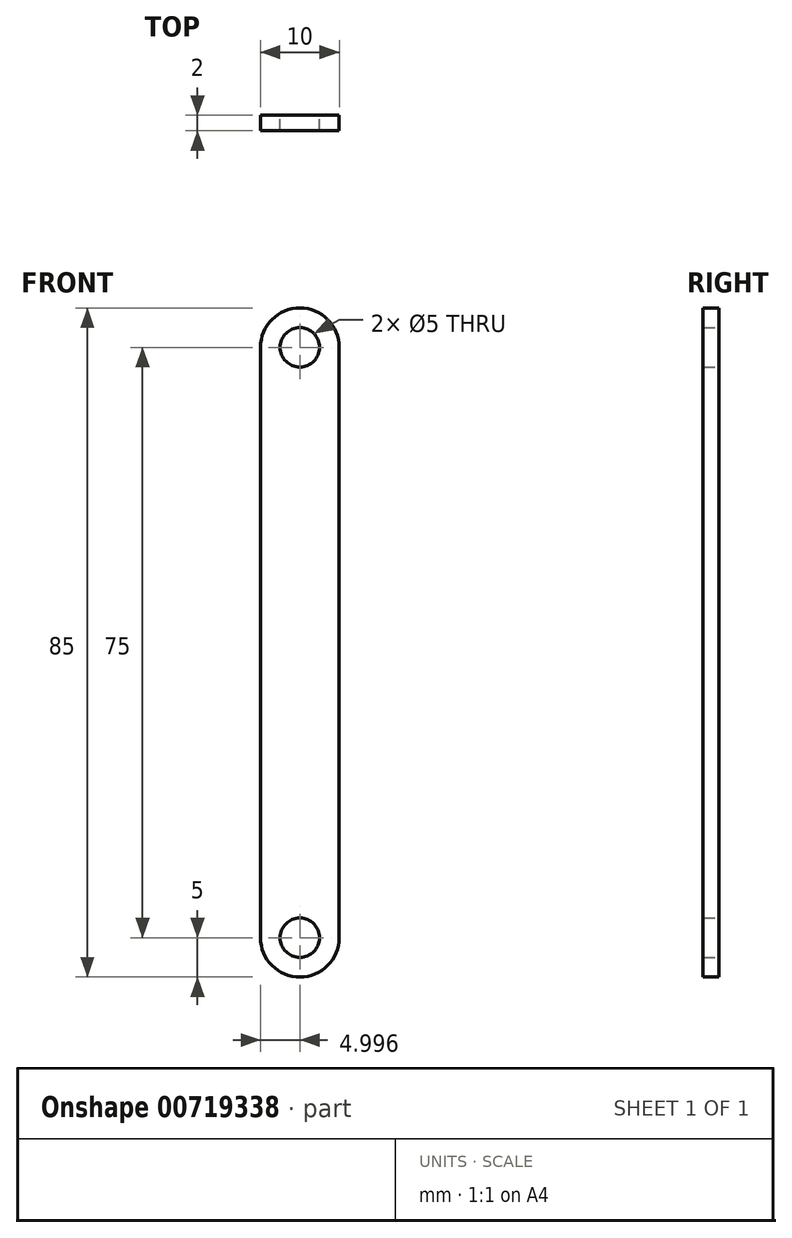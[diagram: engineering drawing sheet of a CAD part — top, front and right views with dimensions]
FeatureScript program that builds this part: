
annotation { "Feature Type Name" : "Feature", "Feature Type Description" : "" }
export const myFeature = defineFeature(function(context is Context, id is Id, definition is map)
    precondition{}
    {
        {
            var Q0;
            Q0=qCreatedBy(makeId("Front.planeOp"),FACE);
            var sketch = newSketch(context, id + "F0", { "sketchPlane" : qUnion([Q0])});
            skLineSegment(sketch, "E0.bottom", {"start": v(4.19, 57.03) * mm, "end": v(4.19, 57.03) * mm});
            skLineSegment(sketch, "E0.top", {"start": v(4.19, -27.97) * mm, "end": v(4.19, -27.97) * mm});
            skLineSegment(sketch, "E0.left", {"start": v(-0.81, 52.03) * mm, "end": v(-0.81, -22.97) * mm});
            skLineSegment(sketch, "E0.right", {"start": v(9.19, 52.03) * mm, "end": v(9.19, -22.97) * mm});
            skPoint(sketch, "E1.visualSharp", {"position": v(-0.81, 57.03) * mm});
            skArc(sketch, "E1.filletArc", {"start": v(4.19, 57.03) * mm, "mid": v(0.65, 55.57) * mm, "end": v(-0.81, 52.03) * mm});
            skPoint(sketch, "E2.visualSharp", {"position": v(9.19, 57.03) * mm});
            skArc(sketch, "E2.filletArc", {"start": v(9.19, 52.03) * mm, "mid": v(7.72, 55.57) * mm, "end": v(4.19, 57.03) * mm});
            skPoint(sketch, "E3.visualSharp", {"position": v(9.19, -27.97) * mm});
            skArc(sketch, "E3.filletArc", {"start": v(4.19, -27.97) * mm, "mid": v(7.72, -26.5) * mm, "end": v(9.19, -22.97) * mm});
            skPoint(sketch, "E4.visualSharp", {"position": v(-0.81, -27.97) * mm});
            skArc(sketch, "E4.filletArc", {"start": v(-0.81, -22.97) * mm, "mid": v(0.65, -26.5) * mm, "end": v(4.19, -27.97) * mm});
            skCircle(sketch, "E5", {"center": v(4.19, 52.03) * mm, "radius": 2.5 * mm});
            skCircle(sketch, "E6", {"center": v(4.19, -22.97) * mm, "radius": 2.5 * mm});
            skSolve(sketch);
        }
        {
            var Q0;
            Q0 = qSketchRegion(id + "F0", true);
            extrude(context, id + "F1", {"entities" : qUnion([Q0]), "depth" : 2 * mm, "offsetDistance" : 25.4 * mm});
        }
    });
